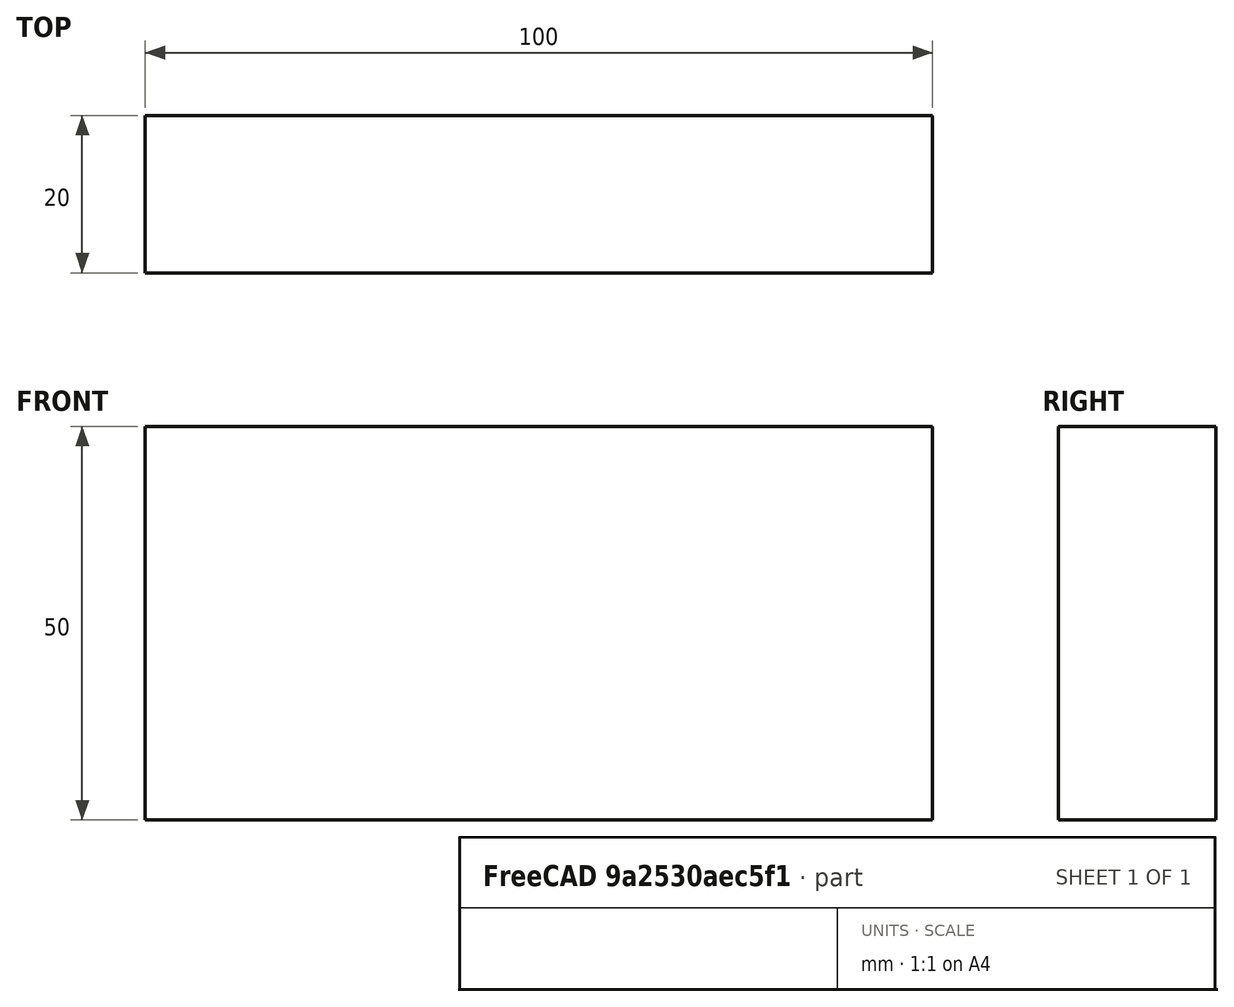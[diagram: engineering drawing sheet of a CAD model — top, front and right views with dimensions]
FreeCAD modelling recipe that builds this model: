
FCSTD DOCUMENT  (FreeCAD 0.15R4671 (Git))
Label: Flat Bar 100x20 EN10058 S235JR
License: All rights reserved
LicenseURL: http://en.wikipedia.org/wiki/All_rights_reserved
objects: Sketcher::SketchObject×1, Part::Extrusion×1
note: 2 computed .brp shape members not serialized (recipe doc carries the construction recipe); baked Part::Feature solids carry a one-line shape summary decoded from their .brp

FEATURE [Sketcher::SketchObject] Sketch
  sketch-geometry (4):
    g0: LineSegment StartX=-50 StartY=-10 StartZ=0 EndX=50 EndY=-10 EndZ=0
    g1: LineSegment StartX=50 StartY=-10 StartZ=0 EndX=50 EndY=10 EndZ=0
    g2: LineSegment StartX=50 StartY=10 StartZ=0 EndX=-50 EndY=10 EndZ=0
    g3: LineSegment StartX=-50 StartY=10 StartZ=0 EndX=-50 EndY=-10 EndZ=0
  constraints (12):
    c: Coincident(g0,g1)
    c: Coincident(g1,g2)
    c: Coincident(g2,g3)
    c: Coincident(g3,g0)
    c: Horizontal(g0)
    c: Horizontal(g2)
    c: Vertical(g1)
    c: Vertical(g3)
    c: Symmetric(g1,g2,g-2)
    c: Symmetric(g0,g1,g-1)
    c: DistanceY(g1) = 20
    c: DistanceX(g0) = 100
FEATURE [Part::Extrusion] Extrude  label="Flat Bar 100x20 EN10058 S235JR"
  Base = -> Sketch
  Dir = (0,0,50)
  Solid = true
